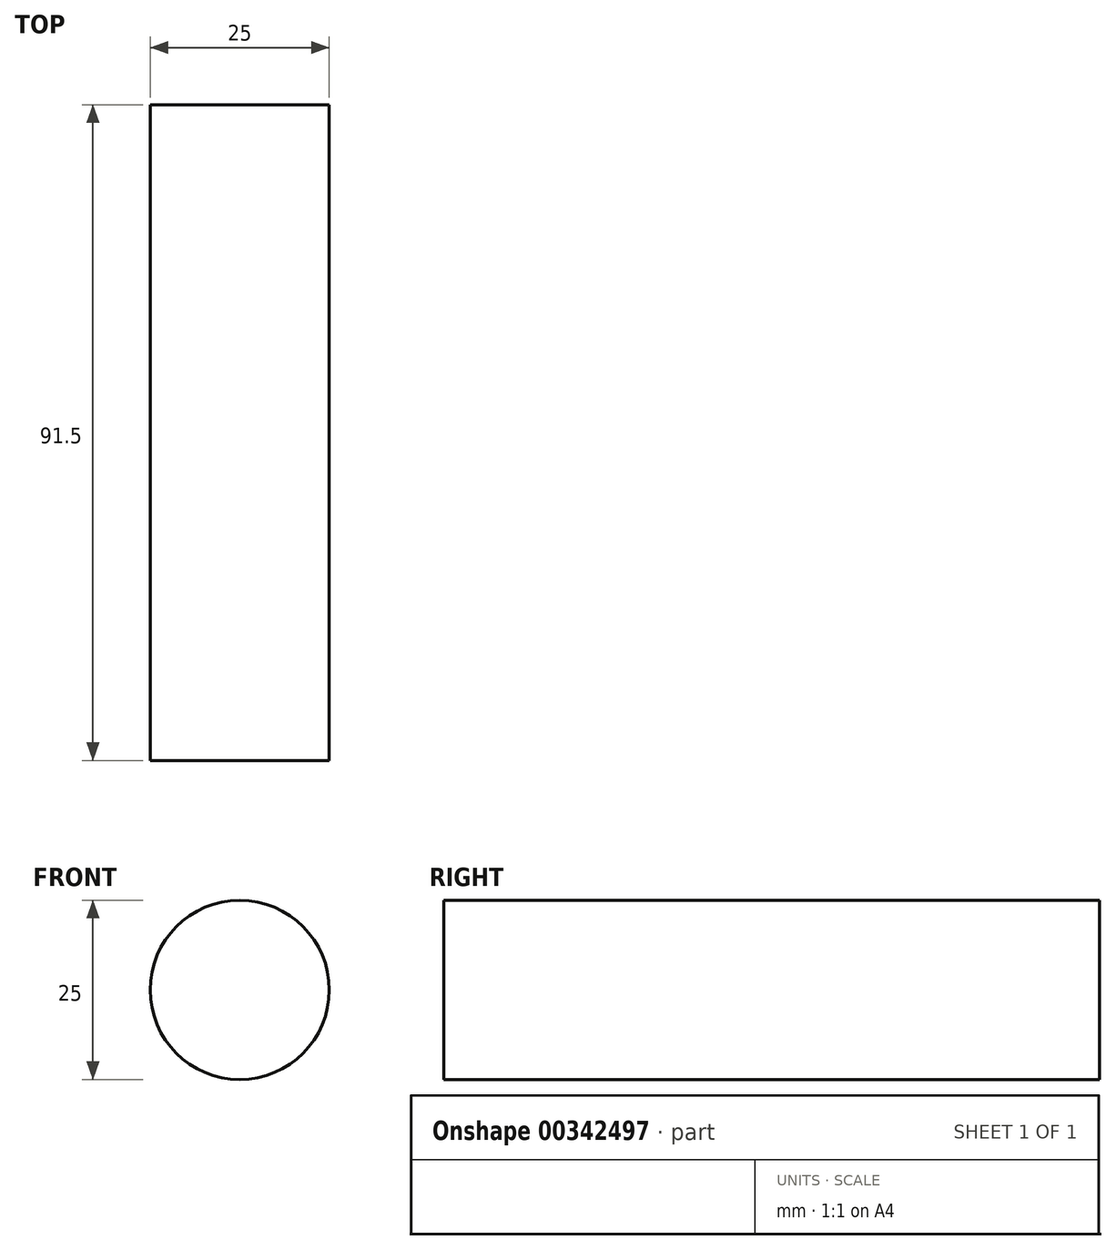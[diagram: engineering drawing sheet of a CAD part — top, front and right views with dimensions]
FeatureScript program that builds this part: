
annotation { "Feature Type Name" : "Feature", "Feature Type Description" : "" }
export const myFeature = defineFeature(function(context is Context, id is Id, definition is map)
    precondition{}
    {
        {
            var Q0;
            Q0=qCreatedBy(makeId("Front.planeOp"),FACE);
            var sketch = newSketch(context, id + "F0", { "sketchPlane" : qUnion([Q0])});
            skCircle(sketch, "E0", {"center": v(0, 0) * mm, "radius": 12.5 * mm});
            skSolve(sketch);
        }
        {
            var Q0;
            Q0=makeQuery(id+"F0.imprint","IMPRINT",FACE,{"disambiguationData":[TD([[makeQuery(id+"F0.imprint","IMPRINT",EDGE,{"derivedFrom":sQuery(id+"F0.wireOp",EDGE,"E0")}),1.0]])]});
            extrude(context, id + "F1", {"entities" : qUnion([Q0]), "depth" : 91.5 * mm, "symmetric" : true});
        }
    });
